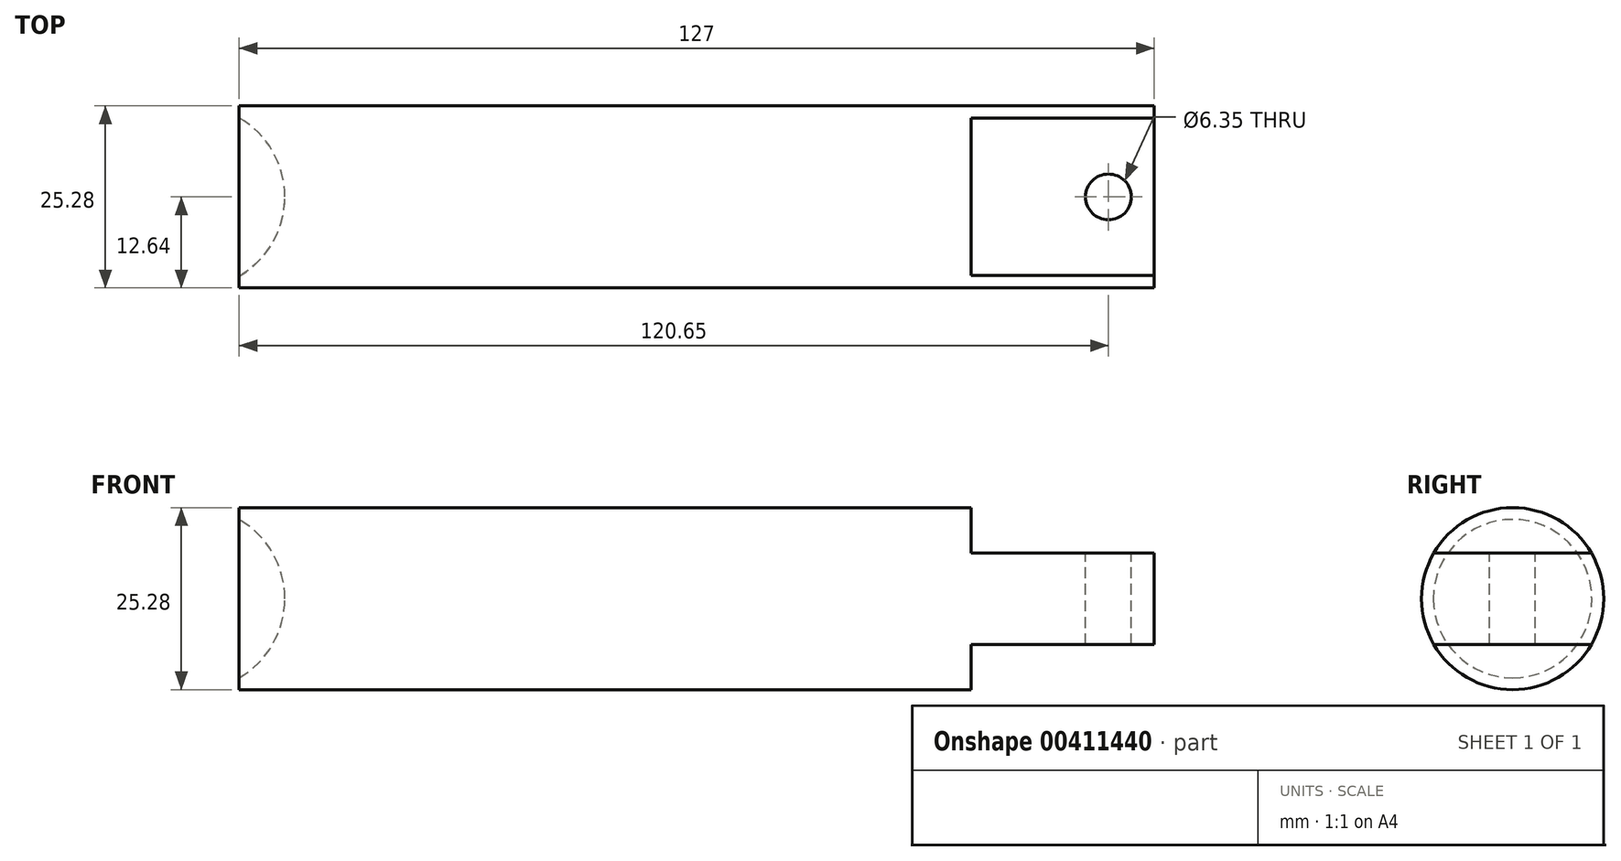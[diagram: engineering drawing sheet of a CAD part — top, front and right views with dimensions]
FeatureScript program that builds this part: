
annotation { "Feature Type Name" : "Feature", "Feature Type Description" : "" }
export const myFeature = defineFeature(function(context is Context, id is Id, definition is map)
    precondition{}
    {
        {
            var Q0;
            Q0=qCreatedBy(makeId("Right.planeOp"),FACE);
            var sketch = newSketch(context, id + "F0", { "sketchPlane" : qUnion([Q0])});
            skCircle(sketch, "E0", {"center": v(0, 0) * mm, "radius": 12.64 * mm});
            skSolve(sketch);
        }
        {
            var Q0;
            Q0=qSketchRegion(id+"F0",true);
            extrude(context, id + "F1", {"entities" : qUnion([Q0]), "endBound" : BoundingType.SYMMETRIC, "depth" : 127 * mm});
        }
        {
            var Q0;
            Q0=qCreatedBy(makeId("Front.planeOp"),FACE);
            var sketch = newSketch(context, id + "F2", { "sketchPlane" : qUnion([Q0])});
            skLineSegment(sketch, "E1", {"start": v(38.1, 12.7) * mm, "end": v(38.1, 6.35) * mm});
            skLineSegment(sketch, "E2", {"start": v(38.1, 6.35) * mm, "end": v(63.5, 6.35) * mm});
            skLineSegment(sketch, "E3", {"start": v(63.5, 6.35) * mm, "end": v(63.5, -6.35) * mm});
            skLineSegment(sketch, "E4", {"start": v(63.5, -6.35) * mm, "end": v(38.1, -6.35) * mm});
            skLineSegment(sketch, "E5", {"start": v(38.1, -6.35) * mm, "end": v(38.1, -12.7) * mm});
            skLineSegment(sketch, "E6", {"start": v(38.1, -12.7) * mm, "end": v(68.58, -12.7) * mm});
            skLineSegment(sketch, "E7", {"start": v(68.58, -12.7) * mm, "end": v(68.58, 12.7) * mm});
            skLineSegment(sketch, "E8", {"start": v(68.58, 12.7) * mm, "end": v(38.1, 12.7) * mm});
            skSolve(sketch);
        }
        {
            var Q0;
            Q0=qSketchRegion(id+"F2",true);
            extrude(context, id + "F3", {"entities" : qUnion([Q0]), "operationType" : NewBodyOperationType.REMOVE, "endBound" : BoundingType.SYMMETRIC, "oppositeDirection" : true, "depth" : 25.4 * mm});
        }
        {
            var Q0;
            Q0=makeQuery(id+"F3.boolean.opBoolean","COPY",FACE,{"derivedFrom":makeQuery(id+"F3.opExtrude","SWEPT_FACE",FACE,{"disambiguationData":[OSD([sQuery(id+"F2.wireOp",EDGE,"E2")])]})});
            var sketch = newSketch(context, id + "F4", { "sketchPlane" : qUnion([Q0])});
            skCircle(sketch, "E9", {"center": v(57.15, 0) * mm, "radius": 3.18 * mm});
            skSolve(sketch);
        }
        {
            var Q0;
            Q0=qSketchRegion(id+"F4",true);
            extrude(context, id + "F5", {"entities" : qUnion([Q0]), "operationType" : NewBodyOperationType.REMOVE, "endBound" : BoundingType.UP_TO_NEXT, "oppositeDirection" : true, "depth" : 25.4 * mm});
        }
        {
            var Q0;
            Q0=qCreatedBy(makeId("Top.planeOp"),FACE);
            var sketch = newSketch(context, id + "F6", { "sketchPlane" : qUnion([Q0])});
            skArc(sketch, "E10", {"start": v(-57.15, 0) * mm, "mid": v(-58.85, 6.35) * mm, "end": v(-63.5, 11) * mm});
            skLineSegment(sketch, "E11", {"start": v(0, 0) * mm, "end": v(-69.85, 0) * mm, "construction": true});
            skLineSegment(sketch, "E12", {"start": v(-63.5, 11) * mm, "end": v(-63.5, 0) * mm});
            skLineSegment(sketch, "E13", {"start": v(-63.5, 0) * mm, "end": v(-57.15, 0) * mm});
            skSolve(sketch);
        }
        {
            var Q0;
            Q0=qSketchRegion(id+"F6",true);
            var Q1;
            Q1=sQuery(id+"F6.wireOp",EDGE,"E11");
            revolve(context, id + "F7", {"operationType" : NewBodyOperationType.REMOVE, "entities" : qUnion([Q0]), "axis" : qUnion([Q1]), "revolveType" : RevolveType.FULL});
        }
    });
